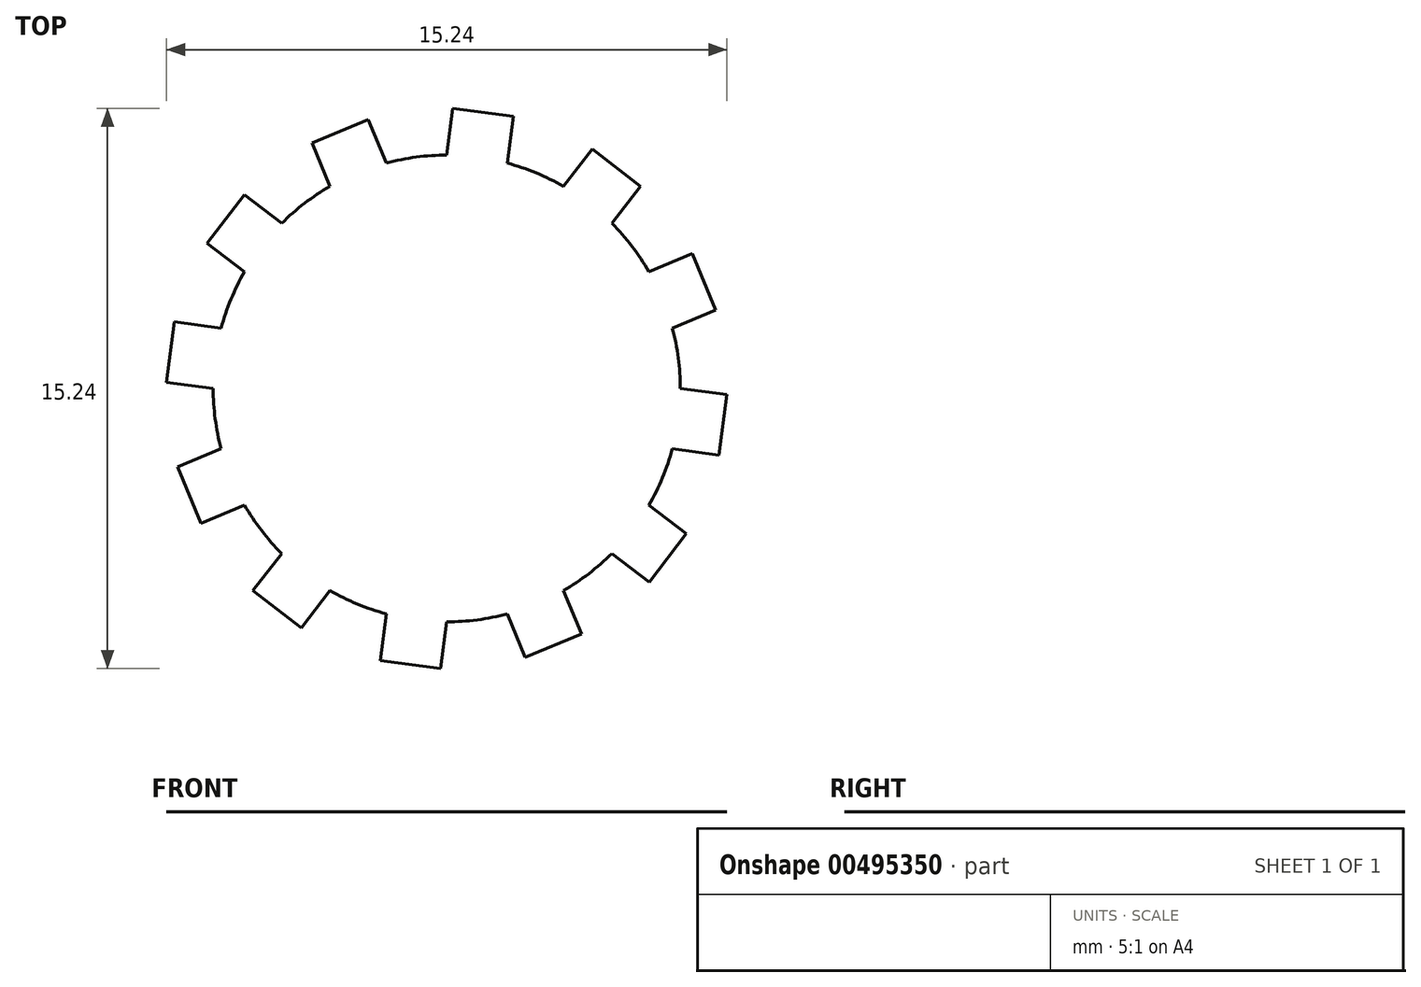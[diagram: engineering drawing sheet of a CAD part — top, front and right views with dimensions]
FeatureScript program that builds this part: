
annotation { "Feature Type Name" : "Feature", "Feature Type Description" : "" }
export const myFeature = defineFeature(function(context is Context, id is Id, definition is map)
    precondition{}
    {
        {
            var Q0;
            Q0=qCreatedBy(makeId("Top.planeOp"),FACE);
            var sketch = newSketch(context, id + "F0", { "sketchPlane" : qUnion([Q0])});
            skCircle(sketch, "E0", {"center": v(0, 0) * mm, "radius": 6.35 * mm});
            skCircle(sketch, "E1", {"center": v(0, 0) * mm, "radius": 7.62 * mm, "construction": true});
            skLineSegment(sketch, "E2", {"start": v(0, 0) * mm, "end": v(0, 23.9) * mm, "construction": true});
            skLineSegment(sketch, "E3", {"start": v(0, 0) * mm, "end": v(12.1, 20.95) * mm, "construction": true});
            skLineSegment(sketch, "E4", {"start": v(0, 0) * mm, "end": v(6.07, 22.66) * mm, "construction": true});
            skLineSegment(sketch, "E5", {"start": v(0, 0) * mm, "end": v(2.8, 21.27) * mm, "construction": true});
            skLineSegment(sketch, "E6", {"start": v(0, 6.35) * mm, "end": v(0.17, 7.62) * mm});
            skLineSegment(sketch, "E7", {"start": v(1.64, 6.13) * mm, "end": v(1.81, 7.4) * mm});
            skLineSegment(sketch, "E8", {"start": v(1.81, 7.4) * mm, "end": v(0.17, 7.62) * mm});
            skSolve(sketch);
        }
        {
            var Q0;
            {var subQ0=sQuery(id+"F0.wireOp",EDGE,"E0");var subQ1=makeQuery(id+"F0.imprint","INTERSECT",VERTEX,{"derivedFrom":[subQ0,sQuery(id+"F0.wireOp",EDGE,"E6")]});Q0=makeQuery(id+"F0.imprint","IMPRINT",FACE,{"disambiguationData":[TD([[makeQuery(id+"F0.imprint","IMPRINT",EDGE,{"disambiguationData":[TD([[subQ1,1.0]])],"derivedFrom":subQ0}),1.0]])]});}
            var Q1;
            {var subQ0=sQuery(id+"F0.wireOp",EDGE,"E6");Q1=makeQuery(id+"F0.imprint","IMPRINT",FACE,{"disambiguationData":[TD([[makeQuery(id+"F0.imprint","IMPRINT",EDGE,{"derivedFrom":subQ0}),-1.0]])]});}
            extrude(context, id + "F1", {"entities" : qUnion([Q0, Q1]), "depth" : 1 / 203.2 * mm});
        }
        {
            var Q0;
            Q0=makeQuery(id+"F1.opExtrude","SWEPT_BODY",BODY,{"disambiguationData":[OSD([sQuery(id+"F0.wireOp",EDGE,"E0"),sQuery(id+"F0.wireOp",EDGE,"E6"),sQuery(id+"F0.wireOp",EDGE,"E7"),sQuery(id+"F0.wireOp",EDGE,"E8")])]});
            var Q1;
            Q1=makeQuery(id+"F1.opExtrude","SWEPT_FACE",FACE,{"disambiguationData":[OSD([sQuery(id+"F0.wireOp",EDGE,"E7")])]});
            var Q2;
            Q2=makeQuery(id+"F1.opExtrude","CAP_FACE",FACE,{"disambiguationData":[OSD([sQuery(id+"F0.wireOp",EDGE,"E0"),sQuery(id+"F0.wireOp",EDGE,"E6"),sQuery(id+"F0.wireOp",EDGE,"E7"),sQuery(id+"F0.wireOp",EDGE,"E8")])],"isStart":false});
            var Q3;
            Q3=makeQuery(id+"F1.opExtrude","SWEPT_FACE",FACE,{"disambiguationData":[OSD([sQuery(id+"F0.wireOp",EDGE,"E8")])]});
            var Q4;
            Q4=makeQuery(id+"F1.opExtrude","CAP_FACE",FACE,{"disambiguationData":[OSD([sQuery(id+"F0.wireOp",EDGE,"E0"),sQuery(id+"F0.wireOp",EDGE,"E6"),sQuery(id+"F0.wireOp",EDGE,"E7"),sQuery(id+"F0.wireOp",EDGE,"E8")])],"isStart":true});
            var Q5;
            Q5=makeQuery(id+"F1.opExtrude","SWEPT_FACE",FACE,{"disambiguationData":[OSD([sQuery(id+"F0.wireOp",EDGE,"E6")])]});
            var Q6;
            Q6=makeQuery(id+"F1.opExtrude","SWEPT_FACE",FACE,{"disambiguationData":[OSD([sQuery(id+"F0.wireOp",EDGE,"E0")])]});
            circularPattern(context, id + "F2", {"operationType" : NewBodyOperationType.ADD, "entities" : qUnion([Q0]), "axis" : qUnion([Q6]), "angle" : 360 * degree, "instanceCount" : 12, "equalSpace" : true});
        }
    });
